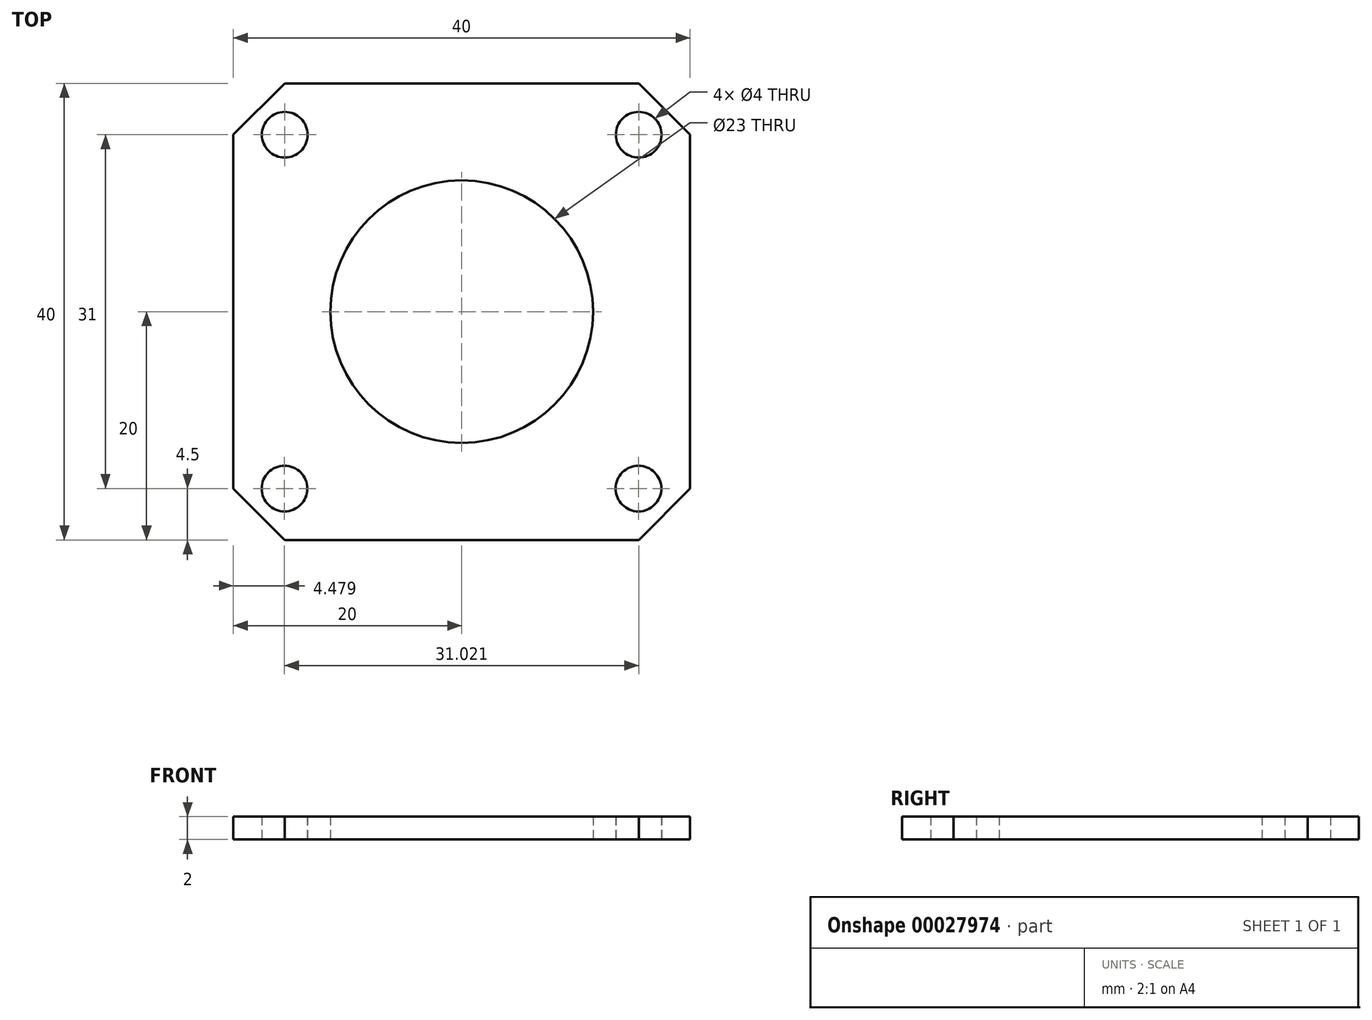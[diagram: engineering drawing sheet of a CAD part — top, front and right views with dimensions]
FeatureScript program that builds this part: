
annotation { "Feature Type Name" : "Feature", "Feature Type Description" : "" }
export const myFeature = defineFeature(function(context is Context, id is Id, definition is map)
    precondition{}
    {
        {
            var Q0;
            Q0=qCreatedBy(makeId("Top.planeOp"),FACE);
            var sketch = newSketch(context, id + "F0", { "sketchPlane" : qUnion([Q0])});
            skLineSegment(sketch, "E0.rect.bottom", {"start": v(20, -20) * mm, "end": v(-20, -20) * mm});
            skLineSegment(sketch, "E0.rect.top", {"start": v(20, 20) * mm, "end": v(-20, 20) * mm});
            skLineSegment(sketch, "E0.rect.left", {"start": v(20, -20) * mm, "end": v(20, 20) * mm});
            skLineSegment(sketch, "E0.rect.right", {"start": v(-20, -20) * mm, "end": v(-20, 20) * mm});
            skPoint(sketch, "E0.rect.middle", {"position": v(0, 0) * mm});
            skLineSegment(sketch, "E1", {"start": v(-25.18, 15.5) * mm, "end": v(25.7, 15.5) * mm, "construction": true});
            skLineSegment(sketch, "E2", {"start": v(-15.5, 24.76) * mm, "end": v(-15.5, -25.85) * mm, "construction": true});
            skLineSegment(sketch, "E3", {"start": v(15.5, 25.66) * mm, "end": v(15.5, -25.72) * mm, "construction": true});
            skLineSegment(sketch, "E4", {"start": v(-26.2, -15.5) * mm, "end": v(25.18, -15.5) * mm, "construction": true});
            skCircle(sketch, "E5", {"center": v(-15.5, 15.5) * mm, "radius": 2 * mm});
            skCircle(sketch, "E6.1.0.0", {"center": v(15.5, 15.5) * mm, "radius": 2 * mm});
            skLineSegment(sketch, "E6.direction1", {"start": v(-15.5, 15.5) * mm, "end": v(15.5, 15.5) * mm, "construction": true});
            skCircle(sketch, "E7.1.0.0", {"center": v(-15.52, -15.5) * mm, "radius": 2 * mm});
            skCircle(sketch, "E7.1.0.1", {"center": v(15.48, -15.5) * mm, "radius": 2 * mm});
            skLineSegment(sketch, "E7.direction1", {"start": v(-15.5, 15.5) * mm, "end": v(-15.52, -15.5) * mm, "construction": true});
            skCircle(sketch, "E8", {"center": v(0, 0) * mm, "radius": 11.5 * mm});
            skSolve(sketch);
        }
        {
            var Q0;
            Q0=makeQuery(id+"F0.imprint","IMPRINT",FACE,{"disambiguationData":[TD([[makeQuery(id+"F0.imprint","IMPRINT",EDGE,{"derivedFrom":sQuery(id+"F0.wireOp",EDGE,"E0.rect.bottom")}),-1.0]])]});
            extrude(context, id + "F1", {"entities" : qUnion([Q0]), "depth" : 2 * mm});
        }
        {
            var Q0;
            Q0=makeQuery(id+"F1.opExtrude","SWEPT_EDGE",EDGE,{"disambiguationData":[OSD([sQuery(id+"F0.wireOp",EDGE,"E0.rect.bottom"),sQuery(id+"F0.wireOp",EDGE,"E0.rect.left")])]});
            var Q1;
            Q1=makeQuery(id+"F1.opExtrude","SWEPT_EDGE",EDGE,{"disambiguationData":[OSD([sQuery(id+"F0.wireOp",EDGE,"E0.rect.top"),sQuery(id+"F0.wireOp",EDGE,"E0.rect.left")])]});
            var Q2;
            Q2=makeQuery(id+"F1.opExtrude","SWEPT_EDGE",EDGE,{"disambiguationData":[OSD([sQuery(id+"F0.wireOp",EDGE,"E0.rect.top"),sQuery(id+"F0.wireOp",EDGE,"E0.rect.right")])]});
            var Q3;
            Q3=makeQuery(id+"F1.opExtrude","SWEPT_EDGE",EDGE,{"disambiguationData":[OSD([sQuery(id+"F0.wireOp",EDGE,"E0.rect.bottom"),sQuery(id+"F0.wireOp",EDGE,"E0.rect.right")])]});
            chamfer(context, id + "F2", {"entities" : qUnion([Q0, Q1, Q2, Q3]), "width" : 4.5 * mm});
        }
    });
